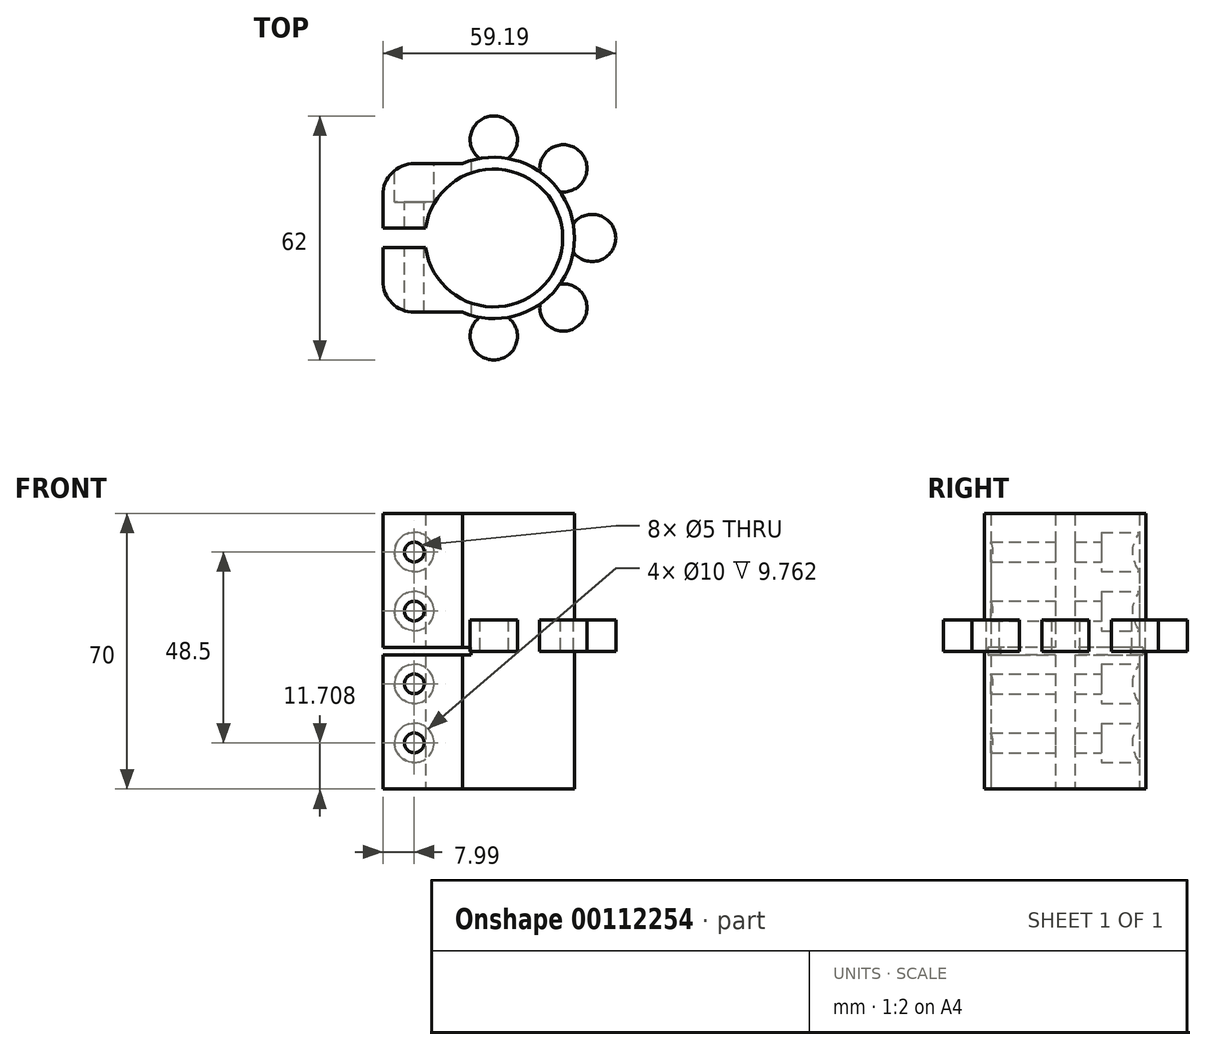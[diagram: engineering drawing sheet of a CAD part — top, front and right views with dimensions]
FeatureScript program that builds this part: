
annotation { "Feature Type Name" : "Feature", "Feature Type Description" : "" }
export const myFeature = defineFeature(function(context is Context, id is Id, definition is map)
    precondition{}
    {
        {
            var Q0;
            Q0=qCreatedBy(makeId("Top.planeOp"),FACE);
            var sketch = newSketch(context, id + "F0", { "sketchPlane" : qUnion([Q0])});
            skArc(sketch, "E0", {"start": v(-20.35, -2.48) * mm, "mid": v(17.74, -10.27) * mm, "end": v(-8, 18.88) * mm});
            skArc(sketch, "E1", {"start": v(-17.32, -2.48) * mm, "mid": v(17.5, 0) * mm, "end": v(-17.32, 2.48) * mm});
            skLineSegment(sketch, "E2", {"start": v(-8, 18.88) * mm, "end": v(-20.2, 18.88) * mm});
            skLineSegment(sketch, "E3", {"start": v(-28.2, 10.88) * mm, "end": v(-28.2, 2.48) * mm});
            skLineSegment(sketch, "E4", {"start": v(-28.2, 2.48) * mm, "end": v(-17.32, 2.48) * mm});
            skPoint(sketch, "E5.visualSharp", {"position": v(-28.2, 18.88) * mm});
            skArc(sketch, "E5.filletArc", {"start": v(-20.2, 18.88) * mm, "mid": v(-25.85, 16.54) * mm, "end": v(-28.2, 10.88) * mm});
            skLineSegment(sketch, "E6", {"start": v(0, 0) * mm, "end": v(49.9, 0) * mm, "construction": true});
            skLineSegment(sketch, "E7.MirrorCS", {"start": v(-28.2, -2.48) * mm, "end": v(-17.32, -2.48) * mm});
            skLineSegment(sketch, "E8.MirrorCS", {"start": v(-8, -18.88) * mm, "end": v(-20.2, -18.88) * mm});
            skLineSegment(sketch, "E9.MirrorCS", {"start": v(-28.2, -10.88) * mm, "end": v(-28.2, -2.48) * mm});
            skArc(sketch, "E10.MirrorCS", {"start": v(-20.2, -18.88) * mm, "mid": v(-25.85, -16.54) * mm, "end": v(-28.2, -10.88) * mm});
            skSolve(sketch);
        }
        {
            var Q0;
            Q0 = qSketchRegion(id + "F0", true);
            extrude(context, id + "F1", {"entities" : qUnion([Q0]), "endBound" : BoundingType.SYMMETRIC, "depth" : 70 * mm});
        }
        {
            var Q0;
            Q0=makeQuery(id+"F1.opExtrude","SWEPT_FACE",FACE,{"disambiguationData":[OSD([sQuery(id+"F0.wireOp",EDGE,"E2")])]});
            var sketch = newSketch(context, id + "F2", { "sketchPlane" : qUnion([Q0])});
            skPoint(sketch, "E11", {"position": v(20.2, -23.3) * mm});
            skPoint(sketch, "E12", {"position": v(20.2, -8.3) * mm});
            skPoint(sketch, "E13", {"position": v(20.2, 10.2) * mm});
            skPoint(sketch, "E14", {"position": v(20.2, 25.2) * mm});
            skSolve(sketch);
        }
        {
            var Q0;
            Q0=sQuery(id+"F2.wireOp",VERTEX,"E11");
            var Q1;
            Q1=sQuery(id+"F2.wireOp",VERTEX,"E12");
            var Q2;
            Q2=sQuery(id+"F2.wireOp",VERTEX,"E13");
            var Q3;
            Q3=sQuery(id+"F2.wireOp",VERTEX,"E14");
            var Q4;
            Q4=makeQuery(id+"F1.opExtrude","SWEPT_BODY",BODY,{"disambiguationData":[OSD([sQuery(id+"F0.wireOp",EDGE,"E0"),sQuery(id+"F0.wireOp",EDGE,"E1"),sQuery(id+"F0.wireOp",EDGE,"E2"),sQuery(id+"F0.wireOp",EDGE,"E3"),sQuery(id+"F0.wireOp",EDGE,"E4"),sQuery(id+"F0.wireOp",EDGE,"E5.filletArc"),sQuery(id+"F0.wireOp",EDGE,"E7.MirrorCS"),sQuery(id+"F0.wireOp",EDGE,"E8.MirrorCS"),sQuery(id+"F0.wireOp",EDGE,"E9.MirrorCS"),sQuery(id+"F0.wireOp",EDGE,"E10.MirrorCS")])]});
            hole(context, id + "F3", {"style" : HoleStyle.C_BORE, "endStyle" : HoleEndStyle.THROUGH, "holeDiameter" : 5 * mm, "cBoreDiameter" : 10 * mm, "cBoreDepth" : 8 * mm, "locations" : qUnion([Q0, Q1, Q2, Q3]), "scope" : qUnion([Q4]), "isTappedThrough" : true});
        }
        {
            var Q0;
            Q0=qCreatedBy(makeId("Front.planeOp"),FACE);
            var sketch = newSketch(context, id + "F4", { "sketchPlane" : qUnion([Q0])});
            skLineSegment(sketch, "E15", {"start": v(-28.2, 1) * mm, "end": v(-28.2, -1) * mm});
            skLineSegment(sketch, "E16", {"start": v(-28.2, -1) * mm, "end": v(-5.8, -1) * mm});
            skLineSegment(sketch, "E17", {"start": v(-5.8, -1) * mm, "end": v(-5.8, 1) * mm});
            skLineSegment(sketch, "E18", {"start": v(-5.8, 1) * mm, "end": v(-28.2, 1) * mm});
            skSolve(sketch);
        }
        {
            var Q0;
            Q0 = qSketchRegion(id + "F4", true);
            extrude(context, id + "F5", {"entities" : qUnion([Q0]), "operationType" : NewBodyOperationType.REMOVE, "endBound" : BoundingType.SYMMETRIC, "oppositeDirection" : true, "depth" : 50 * mm});
        }
        {
            var Q0;
            Q0=qCreatedBy(makeId("Top.planeOp"),FACE);
            var sketch = newSketch(context, id + "F6", { "sketchPlane" : qUnion([Q0])});
            skCircle(sketch, "E19", {"center": v(0, -25) * mm, "radius": 6 * mm});
            skCircle(sketch, "E20.1.0", {"center": v(17.68, -17.68) * mm, "radius": 6 * mm});
            skCircle(sketch, "E20.2.0", {"center": v(25, 0) * mm, "radius": 6 * mm});
            skCircle(sketch, "E20.3.0", {"center": v(17.68, 17.68) * mm, "radius": 6 * mm});
            skCircle(sketch, "E20.4.0", {"center": v(0, 25) * mm, "radius": 6 * mm});
            skPoint(sketch, "E20.center", {"position": v(0, 0) * mm});
            skLineSegment(sketch, "E20.anchor1", {"start": v(0, 0) * mm, "end": v(0, -25) * mm, "construction": true});
            skLineSegment(sketch, "E20.anchor2", {"start": v(0, 0) * mm, "end": v(0, 25) * mm, "construction": true});
            skSolve(sketch);
        }
        {
            var Q0;
            Q0 = qSketchRegion(id + "F6", true);
            extrude(context, id + "F7", {"entities" : qUnion([Q0]), "operationType" : NewBodyOperationType.ADD, "depth" : 8 * mm});
        }
    });
